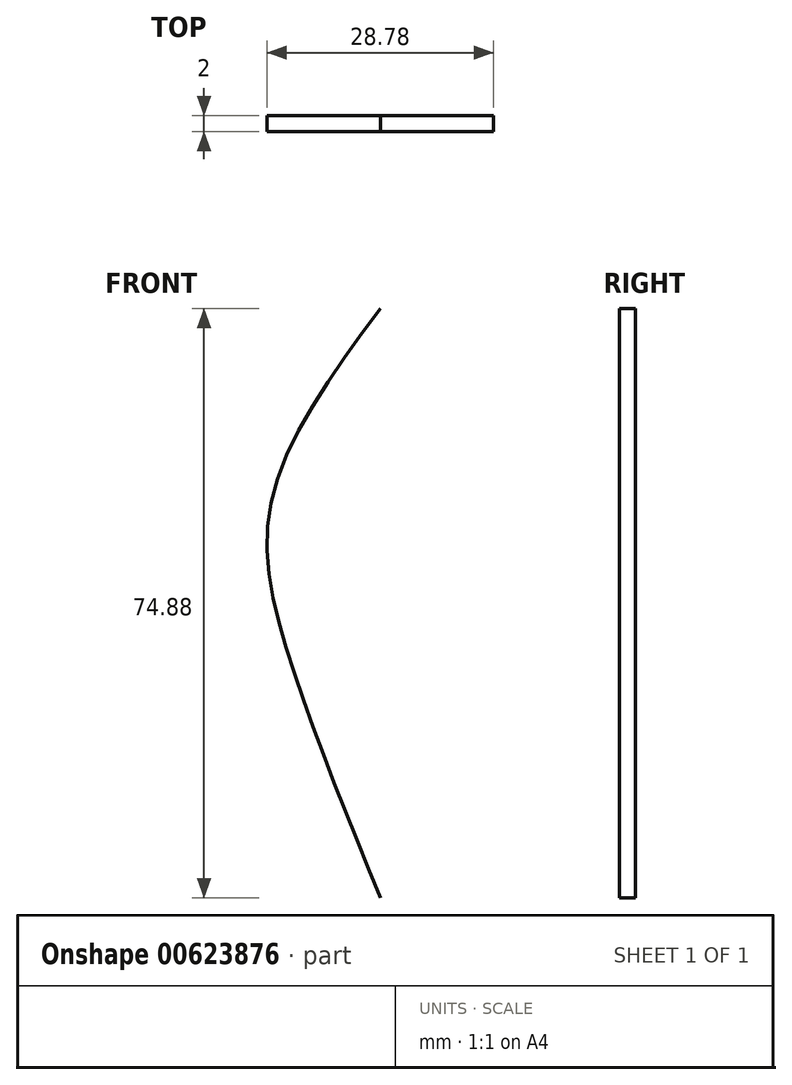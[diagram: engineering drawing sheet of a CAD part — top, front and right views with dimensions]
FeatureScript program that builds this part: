
annotation { "Feature Type Name" : "Feature", "Feature Type Description" : "" }
export const myFeature = defineFeature(function(context is Context, id is Id, definition is map)
    precondition{}
    {
        {
            var Q0;
            Q0=qCreatedBy(makeId("Front.planeOp"),FACE);
            var sketch = newSketch(context, id + "F0", { "sketchPlane" : qUnion([Q0])});
            skFitSpline(sketch, "E0", {"points": [v(0, 0) * mm, v(-11.3, 29.7) * mm, v(-13.77, 50.75) * mm, v(0, 74.88) * mm], "startDerivative": vector(-34.37, 84.89) * mm, "endDerivative": vector(52.84, 71.74) * mm});
            skFitSpline(sketch, "E1.MirrorCS", {"points": [v(0, 0) * mm, v(11.3, 29.7) * mm, v(13.77, 50.75) * mm, v(0, 74.88) * mm], "startDerivative": vector(34.37, 84.89) * mm, "endDerivative": vector(-52.84, 71.74) * mm});
            skSolve(sketch);
        }
        {
            var Q0;
            Q0=makeQuery(id+"F0.imprint","IMPRINT",FACE,{"disambiguationData":[TD([[makeQuery(id+"F0.imprint","IMPRINT",EDGE,{"derivedFrom":sQuery(id+"F0.wireOp",EDGE,"E0")}),-1.0]])]});
            extrude(context, id + "F1", {"entities" : qUnion([Q0]), "depth" : 2 * mm, "offsetDistance" : 25 * mm});
        }
    });
